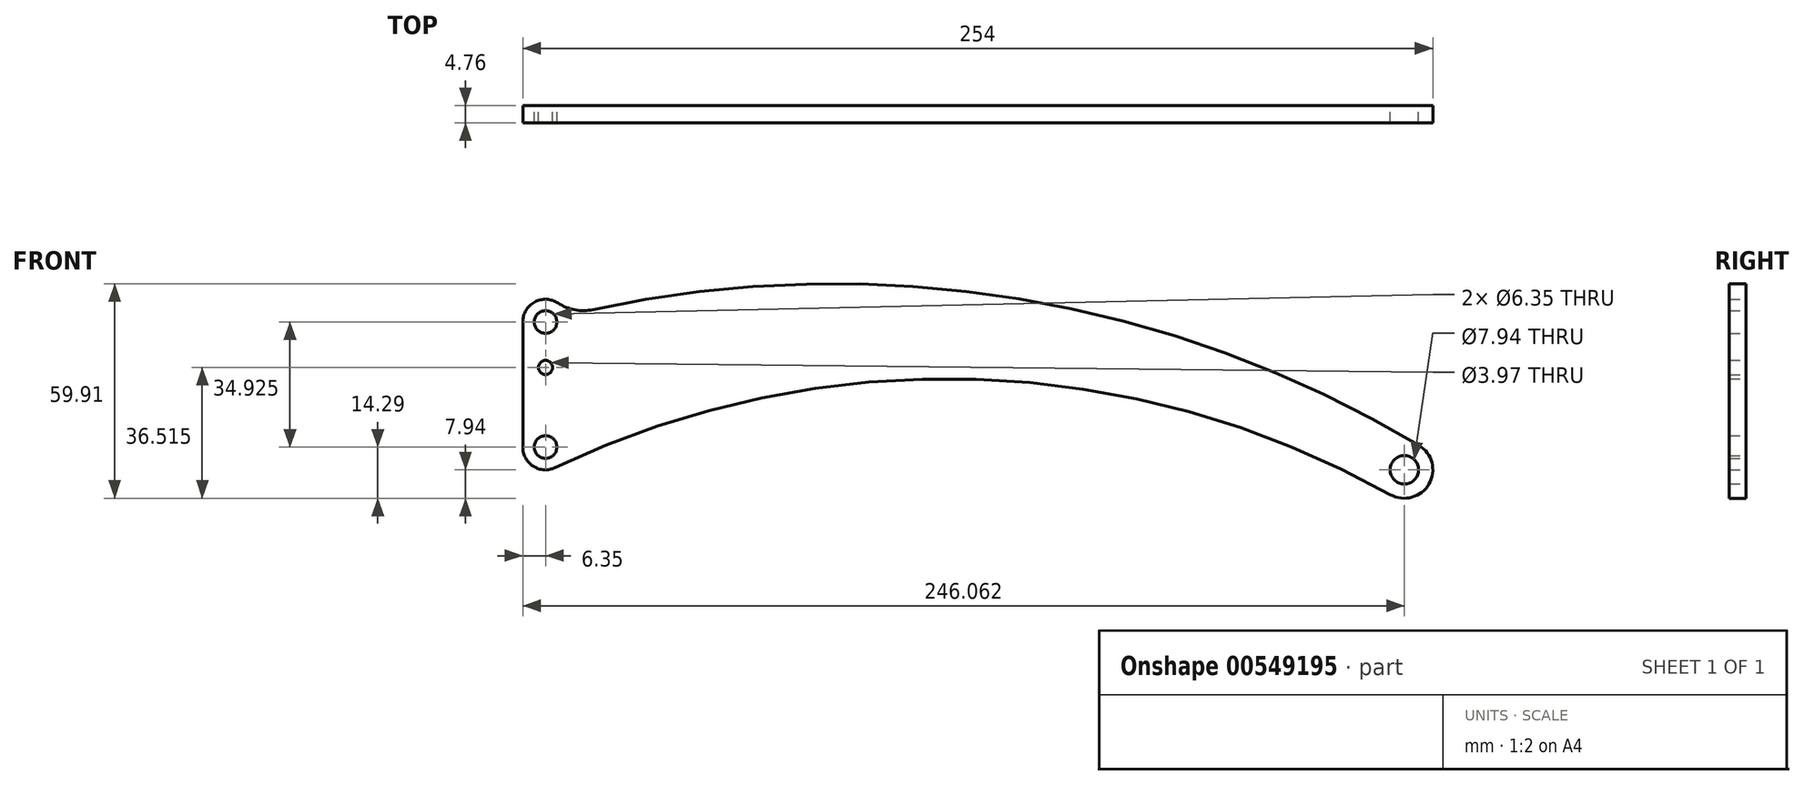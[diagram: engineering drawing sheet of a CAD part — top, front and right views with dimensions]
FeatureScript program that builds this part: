
annotation { "Feature Type Name" : "Feature", "Feature Type Description" : "" }
export const myFeature = defineFeature(function(context is Context, id is Id, definition is map)
    precondition{}
    {
        {
            var Q0;
            Q0=qCreatedBy(makeId("Front.planeOp"),FACE);
            var sketch = newSketch(context, id + "F0", { "sketchPlane" : qUnion([Q0])});
            skLineSegment(sketch, "E0", {"start": v(0, 41.28) * mm, "end": v(0, 6.35) * mm});
            skArc(sketch, "E1", {"start": v(0, 6.35) * mm, "mid": v(2.96, 0.98) * mm, "end": v(9.09, 0.62) * mm});
            skArc(sketch, "E2", {"start": v(242.18, -6.92) * mm, "mid": v(126.56, 25.27) * mm, "end": v(9.09, 0.62) * mm});
            skArc(sketch, "E3", {"start": v(9.86, 46.57) * mm, "mid": v(3.35, 46.87) * mm, "end": v(0, 41.28) * mm});
            skArc(sketch, "E4", {"start": v(242.18, -6.92) * mm, "mid": v(252.93, -3.98) * mm, "end": v(250.14, 6.8) * mm});
            skArc(sketch, "E5", {"start": v(250.14, 6.8) * mm, "mid": v(138.47, 47.76) * mm, "end": v(19.57, 44.74) * mm});
            skArc(sketch, "E6", {"start": v(9.86, 46.57) * mm, "mid": v(14.53, 44.67) * mm, "end": v(19.57, 44.74) * mm});
            skCircle(sketch, "E7", {"center": v(246.06, 0) * mm, "radius": 3.97 * mm});
            skCircle(sketch, "E8", {"center": v(6.35, 6.35) * mm, "radius": 3.18 * mm});
            skCircle(sketch, "E9", {"center": v(6.35, 41.28) * mm, "radius": 3.18 * mm});
            skCircle(sketch, "E10", {"center": v(6.35, 28.58) * mm, "radius": 1.98 * mm});
            skSolve(sketch);
        }
        {
            var Q0;
            Q0=makeQuery(id+"F0.imprint","IMPRINT",FACE,{"disambiguationData":[TD([[makeQuery(id+"F0.imprint","IMPRINT",EDGE,{"derivedFrom":sQuery(id+"F0.wireOp",EDGE,"E0")}),1.0]])]});
            extrude(context, id + "F1", {"entities" : qUnion([Q0]), "depth" : 4.76 * mm, "offsetDistance" : 25.4 * mm});
        }
    });
